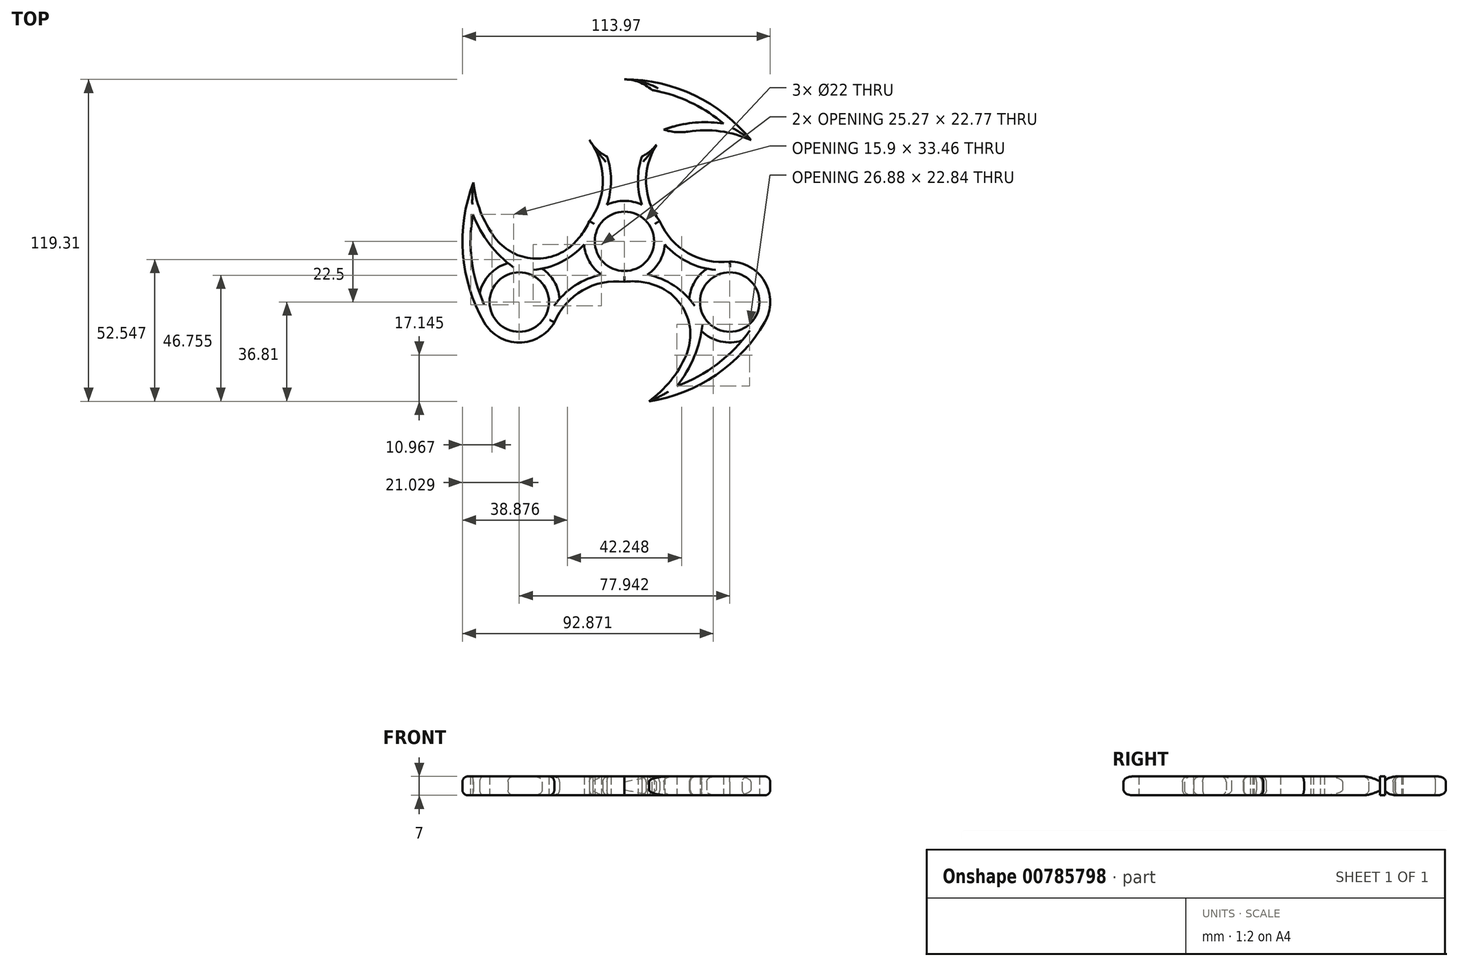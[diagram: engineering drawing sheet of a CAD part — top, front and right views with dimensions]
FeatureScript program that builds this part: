
annotation { "Feature Type Name" : "Feature", "Feature Type Description" : "" }
export const myFeature = defineFeature(function(context is Context, id is Id, definition is map)
    precondition{}
    {
        {
            var Q0;
            Q0=qCreatedBy(makeId("Top.planeOp"),FACE);
            var sketch = newSketch(context, id + "F0", { "sketchPlane" : qUnion([Q0])});
            skCircle(sketch, "E0", {"center": v(0, 0) * mm, "radius": 15 * mm});
            skCircle(sketch, "E1.1.0", {"center": v(0, 45) * mm, "radius": 15 * mm});
            skArc(sketch, "E2", {"start": v(13, 37.5) * mm, "mid": v(8, 22.5) * mm, "end": v(13, 7.5) * mm});
            skArc(sketch, "E3", {"start": v(-13, 7.5) * mm, "mid": v(-8, 22.5) * mm, "end": v(-13, 37.5) * mm});
            skArc(sketch, "E4.1.0", {"start": v(-38.97, -7.5) * mm, "mid": v(-23.48, -4.33) * mm, "end": v(-13, 7.5) * mm});
            skCircle(sketch, "E4.1.1", {"center": v(-38.97, -22.5) * mm, "radius": 15 * mm});
            skArc(sketch, "E4.1.2", {"start": v(0, -15) * mm, "mid": v(-15.5, -18.17) * mm, "end": v(-25.98, -30) * mm});
            skArc(sketch, "E4.2.0", {"start": v(25.98, -30) * mm, "mid": v(15.5, -18.17) * mm, "end": v(0, -15) * mm});
            skCircle(sketch, "E4.2.1", {"center": v(38.97, -22.5) * mm, "radius": 15 * mm});
            skArc(sketch, "E4.2.2", {"start": v(13, 7.5) * mm, "mid": v(23.48, -4.33) * mm, "end": v(38.97, -7.5) * mm});
            skArc(sketch, "E5", {"start": v(46.84, 37.5) * mm, "mid": v(25.98, 54.08) * mm, "end": v(0, 60) * mm});
            skArc(sketch, "E6", {"start": v(46.84, 37.5) * mm, "mid": v(29.91, 41.14) * mm, "end": v(13, 37.5) * mm});
            skArc(sketch, "E7.1.0", {"start": v(-55.9, 21.81) * mm, "mid": v(-50.59, 5.33) * mm, "end": v(-38.97, -7.5) * mm});
            skArc(sketch, "E7.1.1", {"start": v(-55.9, 21.81) * mm, "mid": v(-59.83, -4.54) * mm, "end": v(-51.96, -30) * mm});
            skArc(sketch, "E7.2.0", {"start": v(9.06, -59.31) * mm, "mid": v(20.67, -46.48) * mm, "end": v(25.98, -30) * mm});
            skArc(sketch, "E7.2.1", {"start": v(9.06, -59.31) * mm, "mid": v(33.85, -49.54) * mm, "end": v(51.96, -30) * mm});
            skCircle(sketch, "E8", {"center": v(0, 45) * mm, "radius": 11 * mm});
            skCircle(sketch, "E9", {"center": v(0, 0) * mm, "radius": 11 * mm});
            skCircle(sketch, "E10.1.0", {"center": v(-38.97, -22.5) * mm, "radius": 11 * mm});
            skCircle(sketch, "E10.2.0", {"center": v(38.97, -22.5) * mm, "radius": 11 * mm});
            skArc(sketch, "E11.0", {"start": v(19.43, -53.59) * mm, "mid": v(25.9, -42.64) * mm, "end": v(28.97, -30.3) * mm});
            skArc(sketch, "E11.1", {"start": v(19.43, -53.59) * mm, "mid": v(36.61, -43.69) * mm, "end": v(49.36, -28.5) * mm});
            skArc(sketch, "E12.1.0", {"start": v(36.7, 43.62) * mm, "mid": v(23.98, 43.74) * mm, "end": v(11.76, 40.23) * mm});
            skArc(sketch, "E12.1.1", {"start": v(36.7, 43.62) * mm, "mid": v(19.53, 53.55) * mm, "end": v(0, 57) * mm});
            skArc(sketch, "E12.2.0", {"start": v(-56.12, 9.97) * mm, "mid": v(-49.87, -1.1) * mm, "end": v(-40.72, -9.94) * mm});
            skArc(sketch, "E12.2.1", {"start": v(-56.12, 9.97) * mm, "mid": v(-56.14, -9.86) * mm, "end": v(-49.36, -28.5) * mm});
            skArc(sketch, "E13.0", {"start": v(10.6, 39.3) * mm, "mid": v(5, 22.5) * mm, "end": v(10.6, 5.7) * mm});
            skArc(sketch, "E14.0", {"start": v(-10.6, 5.7) * mm, "mid": v(-5, 22.5) * mm, "end": v(-10.6, 39.3) * mm});
            skArc(sketch, "E15.1.0", {"start": v(0.36, -12.02) * mm, "mid": v(-17, -15.57) * mm, "end": v(-28.74, -28.82) * mm});
            skArc(sketch, "E15.1.1", {"start": v(-39.33, -10.48) * mm, "mid": v(-21.98, -6.93) * mm, "end": v(-10.23, 6.32) * mm});
            skArc(sketch, "E15.2.0", {"start": v(10.23, 6.32) * mm, "mid": v(21.98, -6.93) * mm, "end": v(39.33, -10.48) * mm});
            skArc(sketch, "E15.2.1", {"start": v(28.74, -28.82) * mm, "mid": v(17, -15.57) * mm, "end": v(-0.36, -12.02) * mm});
            skSolve(sketch);
        }
        {
            var Q0;
            {var subQ0=sQuery(id+"F0.wireOp",EDGE,"E2");var subQ1=sQuery(id+"F0.wireOp",EDGE,"E0");var subQ2=makeQuery(id+"F0.imprint","INTERSECT",VERTEX,{"derivedFrom":[subQ1,subQ0]});Q0=makeQuery(id+"F0.imprint","IMPRINT",FACE,{"disambiguationData":[TD([[makeQuery(id+"F0.imprint","IMPRINT",EDGE,{"disambiguationData":[TD([[subQ2,-1.0]])],"derivedFrom":subQ1}),-1.0]])]});}
            var Q1;
            {var subQ1=sQuery(id+"F0.wireOp",EDGE,"E1.1.0");var subQ4=sQuery(id+"F0.wireOp",EDGE,"E3");var subQ7=makeQuery(id+"F0.imprint","INTERSECT",VERTEX,{"disambiguationData":[OD(0.0)],"derivedFrom":[subQ1,subQ4]});Q1=makeQuery(id+"F0.imprint","IMPRINT",FACE,{"disambiguationData":[TD([[makeQuery(id+"F0.imprint","IMPRINT",EDGE,{"disambiguationData":[TD([[subQ7,1.0]])],"derivedFrom":subQ1}),1.0]])]});}
            var Q2;
            {var subQ2=sQuery(id+"F0.wireOp",EDGE,"E5");Q2=makeQuery(id+"F0.imprint","IMPRINT",FACE,{"disambiguationData":[TD([[makeQuery(id+"F0.imprint","IMPRINT",EDGE,{"derivedFrom":subQ2}),1.0]])]});}
            var Q3;
            {var subQ6=sQuery(id+"F0.wireOp",EDGE,"341513d7-6e59-46b0-92f8-b63efdb03c57.3.0");Q3=makeQuery(id+"F0.imprint","IMPRINT",FACE,{"disambiguationData":[TD([[makeQuery(id+"F0.imprint","IMPRINT",EDGE,{"derivedFrom":subQ6}),1.0]])]});}
            var Q4;
            {var subQ5=sQuery(id+"F0.wireOp",EDGE,"341513d7-6e59-46b0-92f8-b63efdb03c57.1.0");Q4=makeQuery(id+"F0.imprint","IMPRINT",FACE,{"disambiguationData":[TD([[makeQuery(id+"F0.imprint","IMPRINT",EDGE,{"derivedFrom":subQ5}),1.0]])]});}
            var Q5;
            {var subQ6=sQuery(id+"F0.wireOp",EDGE,"341513d7-6e59-46b0-92f8-b63efdb03c57.1.0");Q5=makeQuery(id+"F0.imprint","IMPRINT",FACE,{"disambiguationData":[TD([[makeQuery(id+"F0.imprint","IMPRINT",EDGE,{"derivedFrom":subQ6}),-1.0]])]});}
            var Q6;
            {var subQ0=sQuery(id+"F0.wireOp",EDGE,"E4.2.0");var subQ1=sQuery(id+"F0.wireOp",EDGE,"E0");var subQ2=makeQuery(id+"F0.imprint","INTERSECT",VERTEX,{"derivedFrom":[subQ1,subQ0]});Q6=makeQuery(id+"F0.imprint","IMPRINT",FACE,{"disambiguationData":[TD([[makeQuery(id+"F0.imprint","IMPRINT",EDGE,{"disambiguationData":[TD([[subQ2,-1.0]])],"derivedFrom":subQ1}),-1.0]])]});}
            var Q7;
            {var subQ0=sQuery(id+"F0.wireOp",EDGE,"E4.2.1");var subQ4=sQuery(id+"F0.wireOp",EDGE,"E4.2.2");var subQ5=makeQuery(id+"F0.imprint","INTERSECT",VERTEX,{"disambiguationData":[OD(0.0)],"derivedFrom":[subQ0,subQ4]});Q7=makeQuery(id+"F0.imprint","IMPRINT",FACE,{"disambiguationData":[TD([[makeQuery(id+"F0.imprint","IMPRINT",EDGE,{"disambiguationData":[TD([[subQ5,1.0]])],"derivedFrom":subQ0}),1.0]])]});}
            var Q8;
            {var subQ0=sQuery(id+"F0.wireOp",EDGE,"E7.2.0");Q8=makeQuery(id+"F0.imprint","IMPRINT",FACE,{"disambiguationData":[TD([[makeQuery(id+"F0.imprint","IMPRINT",EDGE,{"derivedFrom":subQ0}),-1.0]])]});}
            var Q9;
            {var subQ0=sQuery(id+"F0.wireOp",EDGE,"E4.1.2");var subQ1=sQuery(id+"F0.wireOp",EDGE,"E0");var subQ2=makeQuery(id+"F0.imprint","INTERSECT",VERTEX,{"derivedFrom":[subQ1,subQ0]});Q9=makeQuery(id+"F0.imprint","IMPRINT",FACE,{"disambiguationData":[TD([[makeQuery(id+"F0.imprint","IMPRINT",EDGE,{"disambiguationData":[TD([[subQ2,1.0]])],"derivedFrom":subQ1}),-1.0]])]});}
            var Q10;
            {var subQ0=sQuery(id+"F0.wireOp",EDGE,"E4.1.1");var subQ4=sQuery(id+"F0.wireOp",EDGE,"E4.1.2");var subQ5=makeQuery(id+"F0.imprint","INTERSECT",VERTEX,{"disambiguationData":[OD(0.0)],"derivedFrom":[subQ0,subQ4]});Q10=makeQuery(id+"F0.imprint","IMPRINT",FACE,{"disambiguationData":[TD([[makeQuery(id+"F0.imprint","IMPRINT",EDGE,{"disambiguationData":[TD([[subQ5,1.0]])],"derivedFrom":subQ0}),1.0]])]});}
            var Q11;
            {var subQ0=sQuery(id+"F0.wireOp",EDGE,"E7.1.0");Q11=makeQuery(id+"F0.imprint","IMPRINT",FACE,{"disambiguationData":[TD([[makeQuery(id+"F0.imprint","IMPRINT",EDGE,{"derivedFrom":subQ0}),-1.0]])]});}
            var Q12;
            Q12=makeQuery(id+"F0.imprint","IMPRINT",FACE,{"disambiguationData":[TD([[makeQuery(id+"F0.imprint","IMPRINT",EDGE,{"derivedFrom":sQuery(id+"F0.wireOp",EDGE,"NTt4Oxux-EbMS-pmVs-D787-ScUg5Kec3Hln")}),-1.0]])]});
            var Q13;
            Q13=makeQuery(id+"F0.imprint","IMPRINT",FACE,{"disambiguationData":[TD([[makeQuery(id+"F0.imprint","IMPRINT",EDGE,{"derivedFrom":sQuery(id+"F0.wireOp",EDGE,"E9")}),-1.0]])]});
            var Q14;
            {var subQ0=sQuery(id+"F0.wireOp",EDGE,"E4.1.0");var subQ1=sQuery(id+"F0.wireOp",EDGE,"E0");var subQ2=makeQuery(id+"F0.imprint","INTERSECT",VERTEX,{"derivedFrom":[subQ1,subQ0]});Q14=makeQuery(id+"F0.imprint","IMPRINT",FACE,{"disambiguationData":[TD([[makeQuery(id+"F0.imprint","IMPRINT",EDGE,{"disambiguationData":[TD([[subQ2,-1.0]])],"derivedFrom":subQ1}),-1.0]])]});}
            var Q15;
            {var subQ0=sQuery(id+"F0.wireOp",EDGE,"E3");var subQ1=sQuery(id+"F0.wireOp",EDGE,"E0");var subQ2=makeQuery(id+"F0.imprint","INTERSECT",VERTEX,{"derivedFrom":[subQ1,subQ0]});Q15=makeQuery(id+"F0.imprint","IMPRINT",FACE,{"disambiguationData":[TD([[makeQuery(id+"F0.imprint","IMPRINT",EDGE,{"disambiguationData":[TD([[subQ2,1.0]])],"derivedFrom":subQ1}),-1.0]])]});}
            var Q16;
            {var subQ1=sQuery(id+"F0.wireOp",EDGE,"E3");var subQ2=sQuery(id+"F0.wireOp",EDGE,"E0");var subQ5=makeQuery(id+"F0.imprint","INTERSECT",VERTEX,{"derivedFrom":[subQ2,subQ1]});Q16=makeQuery(id+"F0.imprint","IMPRINT",FACE,{"disambiguationData":[TD([[makeQuery(id+"F0.imprint","IMPRINT",EDGE,{"disambiguationData":[TD([[subQ5,1.0]])],"derivedFrom":subQ2}),1.0]])]});}
            var Q17;
            {var subQ1=sQuery(id+"F0.wireOp",EDGE,"E4.1.2");var subQ2=sQuery(id+"F0.wireOp",EDGE,"E0");var subQ9=makeQuery(id+"F0.imprint","INTERSECT",VERTEX,{"derivedFrom":[subQ2,subQ1]});Q17=makeQuery(id+"F0.imprint","IMPRINT",FACE,{"disambiguationData":[TD([[makeQuery(id+"F0.imprint","IMPRINT",EDGE,{"disambiguationData":[TD([[subQ9,1.0]])],"derivedFrom":subQ2}),1.0]])]});}
            var Q18;
            {var subQ0=sQuery(id+"F0.wireOp",EDGE,"E4.2.2");var subQ2=sQuery(id+"F0.wireOp",EDGE,"E0");var subQ4=makeQuery(id+"F0.imprint","INTERSECT",VERTEX,{"derivedFrom":[subQ2,subQ0]});Q18=makeQuery(id+"F0.imprint","IMPRINT",FACE,{"disambiguationData":[TD([[makeQuery(id+"F0.imprint","IMPRINT",EDGE,{"disambiguationData":[TD([[subQ4,1.0]])],"derivedFrom":subQ2}),1.0]])]});}
            var Q19;
            {var subQ0=sQuery(id+"F0.wireOp",EDGE,"E4.2.2");var subQ1=sQuery(id+"F0.wireOp",EDGE,"E0");var subQ2=makeQuery(id+"F0.imprint","INTERSECT",VERTEX,{"derivedFrom":[subQ1,subQ0]});Q19=makeQuery(id+"F0.imprint","IMPRINT",FACE,{"disambiguationData":[TD([[makeQuery(id+"F0.imprint","IMPRINT",EDGE,{"disambiguationData":[TD([[subQ2,1.0]])],"derivedFrom":subQ1}),-1.0]])]});}
            extrude(context, id + "F1", {"entities" : qUnion([Q0, Q1, Q2, Q3, Q4, Q5, Q6, Q7, Q8, Q9, Q10, Q11, Q12, Q13, Q14, Q15, Q16, Q17, Q18, Q19]), "depth" : 7 * mm, "offsetDistance" : 25 * mm});
        }
        {
            var Q0;
            Q0=makeQuery(id+"F1.opExtrude","SWEPT_EDGE",EDGE,{"disambiguationData":[OSD([sQuery(id+"F0.wireOp",EDGE,"E1.1.0"),sQuery(id+"F0.wireOp",EDGE,"E2"),sQuery(id+"F0.wireOp",EDGE,"E6")])]});
            var Q1;
            Q1=makeQuery(id+"F1.opExtrude","SWEPT_EDGE",EDGE,{"disambiguationData":[OSD([sQuery(id+"F0.wireOp",EDGE,"E4.2.0"),sQuery(id+"F0.wireOp",EDGE,"E4.2.1"),sQuery(id+"F0.wireOp",EDGE,"E7.2.0")])]});
            var Q2;
            Q2=makeQuery(id+"F1.opExtrude","SWEPT_EDGE",EDGE,{"disambiguationData":[OSD([sQuery(id+"F0.wireOp",EDGE,"E4.1.0"),sQuery(id+"F0.wireOp",EDGE,"E4.1.1"),sQuery(id+"F0.wireOp",EDGE,"E7.1.0")])]});
            fillet(context, id + "F2", {"entities" : qUnion([Q0, Q1, Q2]), "radius" : 19.37 * mm, "tangentPropagation" : true, "allowEdgeOverflow" : false});
        }
        {
            var Q0;
            {var subQ0=sQuery(id+"F0.wireOp",EDGE,"E7.1.0");var subQ1=sQuery(id+"F0.wireOp",EDGE,"E4.1.1");var subQ2=sQuery(id+"F0.wireOp",EDGE,"E4.1.0");Q0=makeQuery(id+"F2.opFillet","BLEND_EDGE",EDGE,{"blendedFrom":[makeQuery(id+"F1.opExtrude","SWEPT_EDGE",EDGE,{"disambiguationData":[OSD([subQ2,subQ1,subQ0])]}),makeQuery(id+"F1.opExtrude","CAP_FACE",FACE,{"disambiguationData":[OSD([sQuery(id+"F0.wireOp",EDGE,"E1.1.0"),sQuery(id+"F0.wireOp",EDGE,"E2"),sQuery(id+"F0.wireOp",EDGE,"E3"),subQ2,subQ1,sQuery(id+"F0.wireOp",EDGE,"E4.1.2"),sQuery(id+"F0.wireOp",EDGE,"E4.2.0"),sQuery(id+"F0.wireOp",EDGE,"E4.2.1"),sQuery(id+"F0.wireOp",EDGE,"E4.2.2"),sQuery(id+"F0.wireOp",EDGE,"E5"),sQuery(id+"F0.wireOp",EDGE,"E6"),subQ0,sQuery(id+"F0.wireOp",EDGE,"E7.1.1"),sQuery(id+"F0.wireOp",EDGE,"E7.2.0"),sQuery(id+"F0.wireOp",EDGE,"E7.2.1"),sQuery(id+"F0.wireOp",EDGE,"NTt4Oxux-EbMS-pmVs-D787-ScUg5Kec3Hln"),sQuery(id+"F0.wireOp",EDGE,"FSOzGut8-QLA2-7tGb-JgVf-81xJ9a0HKQdn"),sQuery(id+"F0.wireOp",EDGE,"PodgYQZ9-YV7V-3Zzu-FHNc-UTHKvyW6ABRA"),sQuery(id+"F0.wireOp",EDGE,"QX58wyf9-WBGc-1bDz-3ozh-TM5332mCNNiw")])],"isStart":false})],"blendedInto":[makeQuery(id+"F1.opExtrude","CAP_FACE",FACE,{"disambiguationData":[OSD([sQuery(id+"F0.wireOp",EDGE,"E1.1.0"),sQuery(id+"F0.wireOp",EDGE,"E2"),sQuery(id+"F0.wireOp",EDGE,"E3"),subQ2,subQ1,sQuery(id+"F0.wireOp",EDGE,"E4.1.2"),sQuery(id+"F0.wireOp",EDGE,"E4.2.0"),sQuery(id+"F0.wireOp",EDGE,"E4.2.1"),sQuery(id+"F0.wireOp",EDGE,"E4.2.2"),sQuery(id+"F0.wireOp",EDGE,"E5"),sQuery(id+"F0.wireOp",EDGE,"E6"),subQ0,sQuery(id+"F0.wireOp",EDGE,"E7.1.1"),sQuery(id+"F0.wireOp",EDGE,"E7.2.0"),sQuery(id+"F0.wireOp",EDGE,"E7.2.1"),sQuery(id+"F0.wireOp",EDGE,"NTt4Oxux-EbMS-pmVs-D787-ScUg5Kec3Hln"),sQuery(id+"F0.wireOp",EDGE,"FSOzGut8-QLA2-7tGb-JgVf-81xJ9a0HKQdn"),sQuery(id+"F0.wireOp",EDGE,"PodgYQZ9-YV7V-3Zzu-FHNc-UTHKvyW6ABRA"),sQuery(id+"F0.wireOp",EDGE,"QX58wyf9-WBGc-1bDz-3ozh-TM5332mCNNiw")])],"isStart":false})]});}
            var Q1;
            Q1=makeQuery(id+"F1.opExtrude","CAP_EDGE",EDGE,{"disambiguationData":[OSD([sQuery(id+"F0.wireOp",EDGE,"E7.1.0")])],"isStart":false});
            var Q2;
            Q2=makeQuery(id+"F1.opExtrude","CAP_EDGE",EDGE,{"disambiguationData":[OSD([sQuery(id+"F0.wireOp",EDGE,"E7.1.1")])],"isStart":false});
            var Q3;
            Q3=makeQuery(id+"F1.opExtrude","CAP_EDGE",EDGE,{"disambiguationData":[OSD([sQuery(id+"F0.wireOp",EDGE,"E4.1.1")])],"isStart":false});
            var Q4;
            Q4=makeQuery(id+"F1.opExtrude","CAP_EDGE",EDGE,{"disambiguationData":[OSD([sQuery(id+"F0.wireOp",EDGE,"E4.1.2")])],"isStart":false});
            var Q5;
            Q5=makeQuery(id+"F1.opExtrude","CAP_EDGE",EDGE,{"disambiguationData":[OSD([sQuery(id+"F0.wireOp",EDGE,"E4.2.0")])],"isStart":false});
            var Q6;
            {var subQ0=sQuery(id+"F0.wireOp",EDGE,"E7.2.0");var subQ1=sQuery(id+"F0.wireOp",EDGE,"E4.2.1");var subQ2=sQuery(id+"F0.wireOp",EDGE,"E4.2.0");Q6=makeQuery(id+"F2.opFillet","BLEND_EDGE",EDGE,{"blendedFrom":[makeQuery(id+"F1.opExtrude","SWEPT_EDGE",EDGE,{"disambiguationData":[OSD([subQ2,subQ1,subQ0])]}),makeQuery(id+"F1.opExtrude","CAP_FACE",FACE,{"disambiguationData":[OSD([sQuery(id+"F0.wireOp",EDGE,"E1.1.0"),sQuery(id+"F0.wireOp",EDGE,"E2"),sQuery(id+"F0.wireOp",EDGE,"E3"),sQuery(id+"F0.wireOp",EDGE,"E4.1.0"),sQuery(id+"F0.wireOp",EDGE,"E4.1.1"),sQuery(id+"F0.wireOp",EDGE,"E4.1.2"),subQ2,subQ1,sQuery(id+"F0.wireOp",EDGE,"E4.2.2"),sQuery(id+"F0.wireOp",EDGE,"E5"),sQuery(id+"F0.wireOp",EDGE,"E6"),sQuery(id+"F0.wireOp",EDGE,"E7.1.0"),sQuery(id+"F0.wireOp",EDGE,"E7.1.1"),subQ0,sQuery(id+"F0.wireOp",EDGE,"E7.2.1"),sQuery(id+"F0.wireOp",EDGE,"NTt4Oxux-EbMS-pmVs-D787-ScUg5Kec3Hln"),sQuery(id+"F0.wireOp",EDGE,"FSOzGut8-QLA2-7tGb-JgVf-81xJ9a0HKQdn"),sQuery(id+"F0.wireOp",EDGE,"PodgYQZ9-YV7V-3Zzu-FHNc-UTHKvyW6ABRA"),sQuery(id+"F0.wireOp",EDGE,"QX58wyf9-WBGc-1bDz-3ozh-TM5332mCNNiw")])],"isStart":false})],"blendedInto":[makeQuery(id+"F1.opExtrude","CAP_FACE",FACE,{"disambiguationData":[OSD([sQuery(id+"F0.wireOp",EDGE,"E1.1.0"),sQuery(id+"F0.wireOp",EDGE,"E2"),sQuery(id+"F0.wireOp",EDGE,"E3"),sQuery(id+"F0.wireOp",EDGE,"E4.1.0"),sQuery(id+"F0.wireOp",EDGE,"E4.1.1"),sQuery(id+"F0.wireOp",EDGE,"E4.1.2"),subQ2,subQ1,sQuery(id+"F0.wireOp",EDGE,"E4.2.2"),sQuery(id+"F0.wireOp",EDGE,"E5"),sQuery(id+"F0.wireOp",EDGE,"E6"),sQuery(id+"F0.wireOp",EDGE,"E7.1.0"),sQuery(id+"F0.wireOp",EDGE,"E7.1.1"),subQ0,sQuery(id+"F0.wireOp",EDGE,"E7.2.1"),sQuery(id+"F0.wireOp",EDGE,"NTt4Oxux-EbMS-pmVs-D787-ScUg5Kec3Hln"),sQuery(id+"F0.wireOp",EDGE,"FSOzGut8-QLA2-7tGb-JgVf-81xJ9a0HKQdn"),sQuery(id+"F0.wireOp",EDGE,"PodgYQZ9-YV7V-3Zzu-FHNc-UTHKvyW6ABRA"),sQuery(id+"F0.wireOp",EDGE,"QX58wyf9-WBGc-1bDz-3ozh-TM5332mCNNiw")])],"isStart":false})]});}
            var Q7;
            Q7=makeQuery(id+"F1.opExtrude","CAP_EDGE",EDGE,{"disambiguationData":[OSD([sQuery(id+"F0.wireOp",EDGE,"E7.2.0")])],"isStart":false});
            var Q8;
            Q8=makeQuery(id+"F1.opExtrude","CAP_EDGE",EDGE,{"disambiguationData":[OSD([sQuery(id+"F0.wireOp",EDGE,"E7.2.1")])],"isStart":false});
            var Q9;
            Q9=makeQuery(id+"F1.opExtrude","CAP_EDGE",EDGE,{"disambiguationData":[OSD([sQuery(id+"F0.wireOp",EDGE,"E4.2.1")])],"isStart":false});
            var Q10;
            Q10=makeQuery(id+"F1.opExtrude","CAP_EDGE",EDGE,{"disambiguationData":[OSD([sQuery(id+"F0.wireOp",EDGE,"E4.2.2")])],"isStart":false});
            var Q11;
            Q11=makeQuery(id+"F1.opExtrude","CAP_EDGE",EDGE,{"disambiguationData":[OSD([sQuery(id+"F0.wireOp",EDGE,"E2")])],"isStart":false});
            var Q12;
            {var subQ0=sQuery(id+"F0.wireOp",EDGE,"E6");var subQ1=sQuery(id+"F0.wireOp",EDGE,"E2");var subQ2=sQuery(id+"F0.wireOp",EDGE,"E1.1.0");Q12=makeQuery(id+"F2.opFillet","BLEND_EDGE",EDGE,{"blendedFrom":[makeQuery(id+"F1.opExtrude","SWEPT_EDGE",EDGE,{"disambiguationData":[OSD([subQ2,subQ1,subQ0])]}),makeQuery(id+"F1.opExtrude","CAP_FACE",FACE,{"disambiguationData":[OSD([subQ2,subQ1,sQuery(id+"F0.wireOp",EDGE,"E3"),sQuery(id+"F0.wireOp",EDGE,"E4.1.0"),sQuery(id+"F0.wireOp",EDGE,"E4.1.1"),sQuery(id+"F0.wireOp",EDGE,"E4.1.2"),sQuery(id+"F0.wireOp",EDGE,"E4.2.0"),sQuery(id+"F0.wireOp",EDGE,"E4.2.1"),sQuery(id+"F0.wireOp",EDGE,"E4.2.2"),sQuery(id+"F0.wireOp",EDGE,"E5"),subQ0,sQuery(id+"F0.wireOp",EDGE,"E7.1.0"),sQuery(id+"F0.wireOp",EDGE,"E7.1.1"),sQuery(id+"F0.wireOp",EDGE,"E7.2.0"),sQuery(id+"F0.wireOp",EDGE,"E7.2.1"),sQuery(id+"F0.wireOp",EDGE,"NTt4Oxux-EbMS-pmVs-D787-ScUg5Kec3Hln"),sQuery(id+"F0.wireOp",EDGE,"FSOzGut8-QLA2-7tGb-JgVf-81xJ9a0HKQdn"),sQuery(id+"F0.wireOp",EDGE,"PodgYQZ9-YV7V-3Zzu-FHNc-UTHKvyW6ABRA"),sQuery(id+"F0.wireOp",EDGE,"QX58wyf9-WBGc-1bDz-3ozh-TM5332mCNNiw")])],"isStart":false})],"blendedInto":[makeQuery(id+"F1.opExtrude","CAP_FACE",FACE,{"disambiguationData":[OSD([subQ2,subQ1,sQuery(id+"F0.wireOp",EDGE,"E3"),sQuery(id+"F0.wireOp",EDGE,"E4.1.0"),sQuery(id+"F0.wireOp",EDGE,"E4.1.1"),sQuery(id+"F0.wireOp",EDGE,"E4.1.2"),sQuery(id+"F0.wireOp",EDGE,"E4.2.0"),sQuery(id+"F0.wireOp",EDGE,"E4.2.1"),sQuery(id+"F0.wireOp",EDGE,"E4.2.2"),sQuery(id+"F0.wireOp",EDGE,"E5"),subQ0,sQuery(id+"F0.wireOp",EDGE,"E7.1.0"),sQuery(id+"F0.wireOp",EDGE,"E7.1.1"),sQuery(id+"F0.wireOp",EDGE,"E7.2.0"),sQuery(id+"F0.wireOp",EDGE,"E7.2.1"),sQuery(id+"F0.wireOp",EDGE,"NTt4Oxux-EbMS-pmVs-D787-ScUg5Kec3Hln"),sQuery(id+"F0.wireOp",EDGE,"FSOzGut8-QLA2-7tGb-JgVf-81xJ9a0HKQdn"),sQuery(id+"F0.wireOp",EDGE,"PodgYQZ9-YV7V-3Zzu-FHNc-UTHKvyW6ABRA"),sQuery(id+"F0.wireOp",EDGE,"QX58wyf9-WBGc-1bDz-3ozh-TM5332mCNNiw")])],"isStart":false})]});}
            var Q13;
            Q13=makeQuery(id+"F1.opExtrude","CAP_EDGE",EDGE,{"disambiguationData":[OSD([sQuery(id+"F0.wireOp",EDGE,"E6")])],"isStart":false});
            var Q14;
            Q14=makeQuery(id+"F1.opExtrude","CAP_EDGE",EDGE,{"disambiguationData":[OSD([sQuery(id+"F0.wireOp",EDGE,"E5")])],"isStart":false});
            var Q15;
            Q15=makeQuery(id+"F1.opExtrude","CAP_EDGE",EDGE,{"disambiguationData":[OSD([sQuery(id+"F0.wireOp",EDGE,"E1.1.0")])],"isStart":false});
            var Q16;
            Q16=makeQuery(id+"F1.opExtrude","CAP_EDGE",EDGE,{"disambiguationData":[OSD([sQuery(id+"F0.wireOp",EDGE,"E3")])],"isStart":false});
            var Q17;
            Q17=makeQuery(id+"F1.opExtrude","CAP_EDGE",EDGE,{"disambiguationData":[OSD([sQuery(id+"F0.wireOp",EDGE,"E4.2.2")])],"isStart":true});
            var Q18;
            Q18=makeQuery(id+"F1.opExtrude","CAP_EDGE",EDGE,{"disambiguationData":[OSD([sQuery(id+"F0.wireOp",EDGE,"E4.2.1")])],"isStart":true});
            var Q19;
            Q19=makeQuery(id+"F1.opExtrude","CAP_EDGE",EDGE,{"disambiguationData":[OSD([sQuery(id+"F0.wireOp",EDGE,"E2")])],"isStart":true});
            var Q20;
            {var subQ0=sQuery(id+"F0.wireOp",EDGE,"E6");var subQ1=sQuery(id+"F0.wireOp",EDGE,"E2");var subQ2=sQuery(id+"F0.wireOp",EDGE,"E1.1.0");Q20=makeQuery(id+"F2.opFillet","BLEND_EDGE",EDGE,{"blendedFrom":[makeQuery(id+"F1.opExtrude","SWEPT_EDGE",EDGE,{"disambiguationData":[OSD([subQ2,subQ1,subQ0])]}),makeQuery(id+"F1.opExtrude","CAP_FACE",FACE,{"disambiguationData":[OSD([subQ2,subQ1,sQuery(id+"F0.wireOp",EDGE,"E3"),sQuery(id+"F0.wireOp",EDGE,"E4.1.0"),sQuery(id+"F0.wireOp",EDGE,"E4.1.1"),sQuery(id+"F0.wireOp",EDGE,"E4.1.2"),sQuery(id+"F0.wireOp",EDGE,"E4.2.0"),sQuery(id+"F0.wireOp",EDGE,"E4.2.1"),sQuery(id+"F0.wireOp",EDGE,"E4.2.2"),sQuery(id+"F0.wireOp",EDGE,"E5"),subQ0,sQuery(id+"F0.wireOp",EDGE,"E7.1.0"),sQuery(id+"F0.wireOp",EDGE,"E7.1.1"),sQuery(id+"F0.wireOp",EDGE,"E7.2.0"),sQuery(id+"F0.wireOp",EDGE,"E7.2.1"),sQuery(id+"F0.wireOp",EDGE,"NTt4Oxux-EbMS-pmVs-D787-ScUg5Kec3Hln"),sQuery(id+"F0.wireOp",EDGE,"FSOzGut8-QLA2-7tGb-JgVf-81xJ9a0HKQdn"),sQuery(id+"F0.wireOp",EDGE,"PodgYQZ9-YV7V-3Zzu-FHNc-UTHKvyW6ABRA"),sQuery(id+"F0.wireOp",EDGE,"QX58wyf9-WBGc-1bDz-3ozh-TM5332mCNNiw")])],"isStart":true})],"blendedInto":[makeQuery(id+"F1.opExtrude","CAP_FACE",FACE,{"disambiguationData":[OSD([subQ2,subQ1,sQuery(id+"F0.wireOp",EDGE,"E3"),sQuery(id+"F0.wireOp",EDGE,"E4.1.0"),sQuery(id+"F0.wireOp",EDGE,"E4.1.1"),sQuery(id+"F0.wireOp",EDGE,"E4.1.2"),sQuery(id+"F0.wireOp",EDGE,"E4.2.0"),sQuery(id+"F0.wireOp",EDGE,"E4.2.1"),sQuery(id+"F0.wireOp",EDGE,"E4.2.2"),sQuery(id+"F0.wireOp",EDGE,"E5"),subQ0,sQuery(id+"F0.wireOp",EDGE,"E7.1.0"),sQuery(id+"F0.wireOp",EDGE,"E7.1.1"),sQuery(id+"F0.wireOp",EDGE,"E7.2.0"),sQuery(id+"F0.wireOp",EDGE,"E7.2.1"),sQuery(id+"F0.wireOp",EDGE,"NTt4Oxux-EbMS-pmVs-D787-ScUg5Kec3Hln"),sQuery(id+"F0.wireOp",EDGE,"FSOzGut8-QLA2-7tGb-JgVf-81xJ9a0HKQdn"),sQuery(id+"F0.wireOp",EDGE,"PodgYQZ9-YV7V-3Zzu-FHNc-UTHKvyW6ABRA"),sQuery(id+"F0.wireOp",EDGE,"QX58wyf9-WBGc-1bDz-3ozh-TM5332mCNNiw")])],"isStart":true})]});}
            var Q21;
            Q21=makeQuery(id+"F1.opExtrude","CAP_EDGE",EDGE,{"disambiguationData":[OSD([sQuery(id+"F0.wireOp",EDGE,"E5")])],"isStart":true});
            var Q22;
            Q22=makeQuery(id+"F1.opExtrude","CAP_EDGE",EDGE,{"disambiguationData":[OSD([sQuery(id+"F0.wireOp",EDGE,"E1.1.0")])],"isStart":true});
            var Q23;
            Q23=makeQuery(id+"F1.opExtrude","CAP_EDGE",EDGE,{"disambiguationData":[OSD([sQuery(id+"F0.wireOp",EDGE,"E3")])],"isStart":true});
            var Q24;
            Q24=makeQuery(id+"F1.opExtrude","CAP_EDGE",EDGE,{"disambiguationData":[OSD([sQuery(id+"F0.wireOp",EDGE,"E4.1.0")])],"isStart":true});
            var Q25;
            {var subQ0=sQuery(id+"F0.wireOp",EDGE,"E7.1.0");var subQ1=sQuery(id+"F0.wireOp",EDGE,"E4.1.1");var subQ2=sQuery(id+"F0.wireOp",EDGE,"E4.1.0");Q25=makeQuery(id+"F2.opFillet","BLEND_EDGE",EDGE,{"blendedFrom":[makeQuery(id+"F1.opExtrude","SWEPT_EDGE",EDGE,{"disambiguationData":[OSD([subQ2,subQ1,subQ0])]}),makeQuery(id+"F1.opExtrude","CAP_FACE",FACE,{"disambiguationData":[OSD([sQuery(id+"F0.wireOp",EDGE,"E1.1.0"),sQuery(id+"F0.wireOp",EDGE,"E2"),sQuery(id+"F0.wireOp",EDGE,"E3"),subQ2,subQ1,sQuery(id+"F0.wireOp",EDGE,"E4.1.2"),sQuery(id+"F0.wireOp",EDGE,"E4.2.0"),sQuery(id+"F0.wireOp",EDGE,"E4.2.1"),sQuery(id+"F0.wireOp",EDGE,"E4.2.2"),sQuery(id+"F0.wireOp",EDGE,"E5"),sQuery(id+"F0.wireOp",EDGE,"E6"),subQ0,sQuery(id+"F0.wireOp",EDGE,"E7.1.1"),sQuery(id+"F0.wireOp",EDGE,"E7.2.0"),sQuery(id+"F0.wireOp",EDGE,"E7.2.1"),sQuery(id+"F0.wireOp",EDGE,"NTt4Oxux-EbMS-pmVs-D787-ScUg5Kec3Hln"),sQuery(id+"F0.wireOp",EDGE,"FSOzGut8-QLA2-7tGb-JgVf-81xJ9a0HKQdn"),sQuery(id+"F0.wireOp",EDGE,"PodgYQZ9-YV7V-3Zzu-FHNc-UTHKvyW6ABRA"),sQuery(id+"F0.wireOp",EDGE,"QX58wyf9-WBGc-1bDz-3ozh-TM5332mCNNiw")])],"isStart":true})],"blendedInto":[makeQuery(id+"F1.opExtrude","CAP_FACE",FACE,{"disambiguationData":[OSD([sQuery(id+"F0.wireOp",EDGE,"E1.1.0"),sQuery(id+"F0.wireOp",EDGE,"E2"),sQuery(id+"F0.wireOp",EDGE,"E3"),subQ2,subQ1,sQuery(id+"F0.wireOp",EDGE,"E4.1.2"),sQuery(id+"F0.wireOp",EDGE,"E4.2.0"),sQuery(id+"F0.wireOp",EDGE,"E4.2.1"),sQuery(id+"F0.wireOp",EDGE,"E4.2.2"),sQuery(id+"F0.wireOp",EDGE,"E5"),sQuery(id+"F0.wireOp",EDGE,"E6"),subQ0,sQuery(id+"F0.wireOp",EDGE,"E7.1.1"),sQuery(id+"F0.wireOp",EDGE,"E7.2.0"),sQuery(id+"F0.wireOp",EDGE,"E7.2.1"),sQuery(id+"F0.wireOp",EDGE,"NTt4Oxux-EbMS-pmVs-D787-ScUg5Kec3Hln"),sQuery(id+"F0.wireOp",EDGE,"FSOzGut8-QLA2-7tGb-JgVf-81xJ9a0HKQdn"),sQuery(id+"F0.wireOp",EDGE,"PodgYQZ9-YV7V-3Zzu-FHNc-UTHKvyW6ABRA"),sQuery(id+"F0.wireOp",EDGE,"QX58wyf9-WBGc-1bDz-3ozh-TM5332mCNNiw")])],"isStart":true})]});}
            var Q26;
            Q26=makeQuery(id+"F1.opExtrude","CAP_EDGE",EDGE,{"disambiguationData":[OSD([sQuery(id+"F0.wireOp",EDGE,"E7.1.1")])],"isStart":true});
            var Q27;
            Q27=makeQuery(id+"F1.opExtrude","CAP_EDGE",EDGE,{"disambiguationData":[OSD([sQuery(id+"F0.wireOp",EDGE,"E7.1.0")])],"isStart":true});
            var Q28;
            Q28=makeQuery(id+"F1.opExtrude","CAP_EDGE",EDGE,{"disambiguationData":[OSD([sQuery(id+"F0.wireOp",EDGE,"E4.1.1")])],"isStart":true});
            var Q29;
            Q29=makeQuery(id+"F1.opExtrude","CAP_EDGE",EDGE,{"disambiguationData":[OSD([sQuery(id+"F0.wireOp",EDGE,"E4.1.2")])],"isStart":true});
            var Q30;
            Q30=makeQuery(id+"F1.opExtrude","CAP_EDGE",EDGE,{"disambiguationData":[OSD([sQuery(id+"F0.wireOp",EDGE,"E4.2.0")])],"isStart":true});
            var Q31;
            {var subQ0=sQuery(id+"F0.wireOp",EDGE,"E7.2.0");var subQ1=sQuery(id+"F0.wireOp",EDGE,"E4.2.1");var subQ2=sQuery(id+"F0.wireOp",EDGE,"E4.2.0");Q31=makeQuery(id+"F2.opFillet","BLEND_EDGE",EDGE,{"blendedFrom":[makeQuery(id+"F1.opExtrude","SWEPT_EDGE",EDGE,{"disambiguationData":[OSD([subQ2,subQ1,subQ0])]}),makeQuery(id+"F1.opExtrude","CAP_FACE",FACE,{"disambiguationData":[OSD([sQuery(id+"F0.wireOp",EDGE,"E1.1.0"),sQuery(id+"F0.wireOp",EDGE,"E2"),sQuery(id+"F0.wireOp",EDGE,"E3"),sQuery(id+"F0.wireOp",EDGE,"E4.1.0"),sQuery(id+"F0.wireOp",EDGE,"E4.1.1"),sQuery(id+"F0.wireOp",EDGE,"E4.1.2"),subQ2,subQ1,sQuery(id+"F0.wireOp",EDGE,"E4.2.2"),sQuery(id+"F0.wireOp",EDGE,"E5"),sQuery(id+"F0.wireOp",EDGE,"E6"),sQuery(id+"F0.wireOp",EDGE,"E7.1.0"),sQuery(id+"F0.wireOp",EDGE,"E7.1.1"),subQ0,sQuery(id+"F0.wireOp",EDGE,"E7.2.1"),sQuery(id+"F0.wireOp",EDGE,"NTt4Oxux-EbMS-pmVs-D787-ScUg5Kec3Hln"),sQuery(id+"F0.wireOp",EDGE,"FSOzGut8-QLA2-7tGb-JgVf-81xJ9a0HKQdn"),sQuery(id+"F0.wireOp",EDGE,"PodgYQZ9-YV7V-3Zzu-FHNc-UTHKvyW6ABRA"),sQuery(id+"F0.wireOp",EDGE,"QX58wyf9-WBGc-1bDz-3ozh-TM5332mCNNiw")])],"isStart":true})],"blendedInto":[makeQuery(id+"F1.opExtrude","CAP_FACE",FACE,{"disambiguationData":[OSD([sQuery(id+"F0.wireOp",EDGE,"E1.1.0"),sQuery(id+"F0.wireOp",EDGE,"E2"),sQuery(id+"F0.wireOp",EDGE,"E3"),sQuery(id+"F0.wireOp",EDGE,"E4.1.0"),sQuery(id+"F0.wireOp",EDGE,"E4.1.1"),sQuery(id+"F0.wireOp",EDGE,"E4.1.2"),subQ2,subQ1,sQuery(id+"F0.wireOp",EDGE,"E4.2.2"),sQuery(id+"F0.wireOp",EDGE,"E5"),sQuery(id+"F0.wireOp",EDGE,"E6"),sQuery(id+"F0.wireOp",EDGE,"E7.1.0"),sQuery(id+"F0.wireOp",EDGE,"E7.1.1"),subQ0,sQuery(id+"F0.wireOp",EDGE,"E7.2.1"),sQuery(id+"F0.wireOp",EDGE,"NTt4Oxux-EbMS-pmVs-D787-ScUg5Kec3Hln"),sQuery(id+"F0.wireOp",EDGE,"FSOzGut8-QLA2-7tGb-JgVf-81xJ9a0HKQdn"),sQuery(id+"F0.wireOp",EDGE,"PodgYQZ9-YV7V-3Zzu-FHNc-UTHKvyW6ABRA"),sQuery(id+"F0.wireOp",EDGE,"QX58wyf9-WBGc-1bDz-3ozh-TM5332mCNNiw")])],"isStart":true})]});}
            var Q32;
            Q32=makeQuery(id+"F1.opExtrude","CAP_EDGE",EDGE,{"disambiguationData":[OSD([sQuery(id+"F0.wireOp",EDGE,"E6")])],"isStart":true});
            var Q33;
            Q33=makeQuery(id+"F1.opExtrude","CAP_EDGE",EDGE,{"disambiguationData":[OSD([sQuery(id+"F0.wireOp",EDGE,"E7.2.0")])],"isStart":true});
            var Q34;
            Q34=makeQuery(id+"F1.opExtrude","CAP_EDGE",EDGE,{"disambiguationData":[OSD([sQuery(id+"F0.wireOp",EDGE,"E7.2.1")])],"isStart":true});
            var Q35;
            Q35=makeQuery(id+"F1.opExtrude","CAP_EDGE",EDGE,{"disambiguationData":[OSD([sQuery(id+"F0.wireOp",EDGE,"E4.1.0")])],"isStart":false});
            fillet(context, id + "F3", {"entities" : qUnion([Q0, Q1, Q2, Q3, Q4, Q5, Q6, Q7, Q8, Q9, Q10, Q11, Q12, Q13, Q14, Q15, Q16, Q17, Q18, Q19, Q20, Q21, Q22, Q23, Q24, Q25, Q26, Q27, Q28, Q29, Q30, Q31, Q32, Q33, Q34, Q35]), "radius" : 2 * mm, "tangentPropagation" : true, "allowEdgeOverflow" : false});
        }
    });
